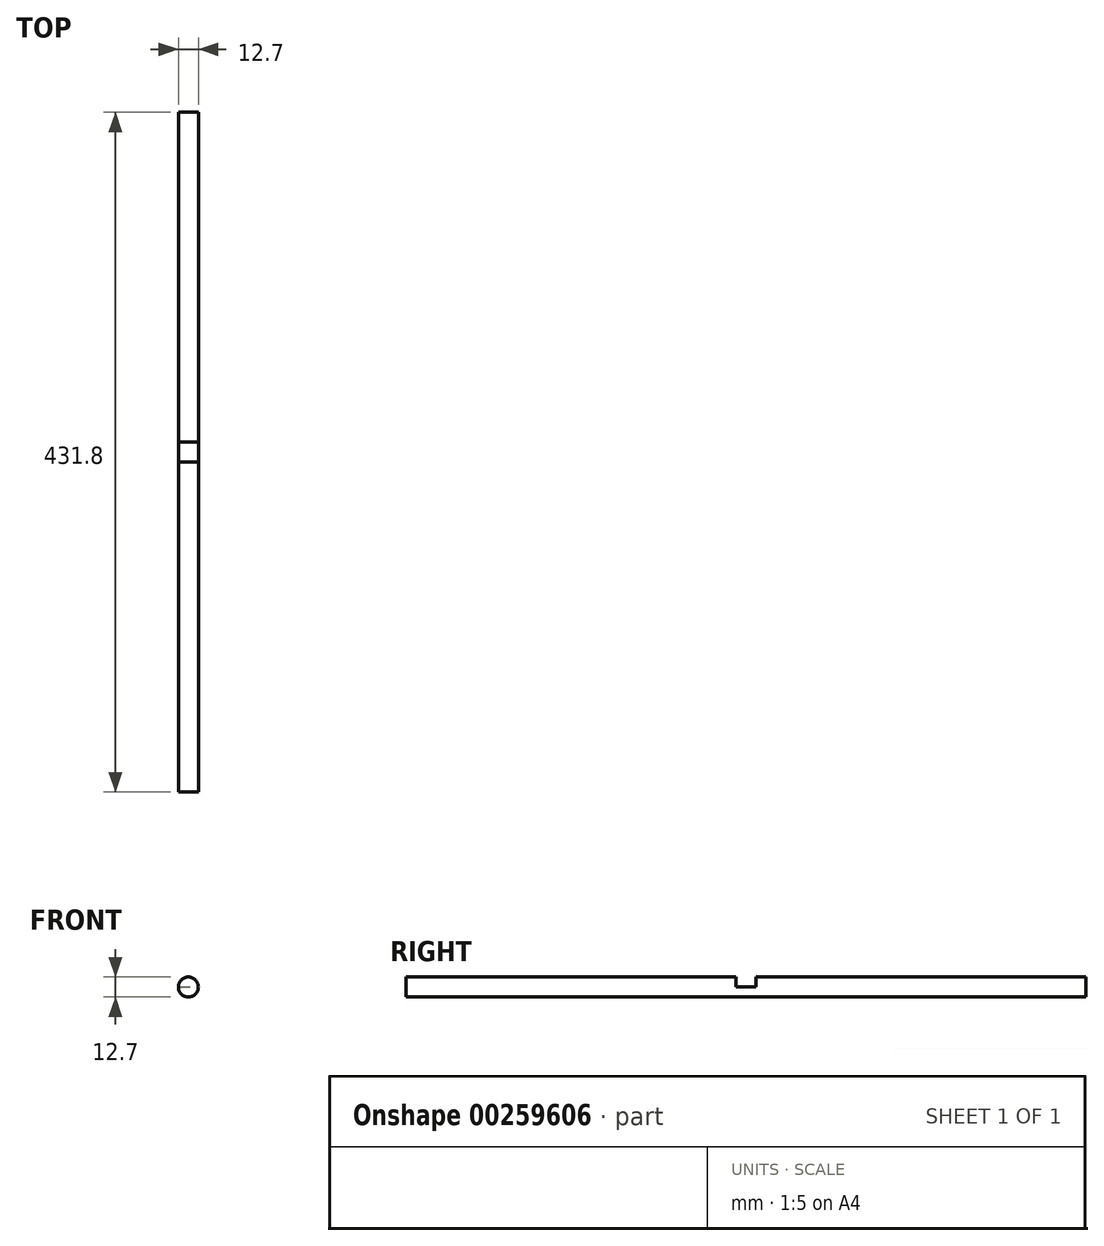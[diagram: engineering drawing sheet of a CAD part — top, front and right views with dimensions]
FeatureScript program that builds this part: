
annotation { "Feature Type Name" : "Feature", "Feature Type Description" : "" }
export const myFeature = defineFeature(function(context is Context, id is Id, definition is map)
    precondition{}
    {
        {
            var Q0;
            Q0=qCreatedBy(makeId("Front.planeOp"),FACE);
            var sketch = newSketch(context, id + "F0", { "sketchPlane" : qUnion([Q0])});
            skCircle(sketch, "E0", {"center": v(0, 0) * mm, "radius": 6.35 * mm});
            skSolve(sketch);
        }
        {
            var Q0;
            Q0=makeQuery(id+"F0.imprint","IMPRINT",FACE,{"disambiguationData":[TD([[makeQuery(id+"F0.imprint","IMPRINT",EDGE,{"derivedFrom":sQuery(id+"F0.wireOp",EDGE,"E0")}),1.0]])]});
            extrude(context, id + "F1", {"entities" : qUnion([Q0]), "depth" : 431.8 * mm, "symmetric" : true});
        }
        {
            var Q0;
            Q0=qCreatedBy(makeId("Right.planeOp"),FACE);
            var sketch = newSketch(context, id + "F2", { "sketchPlane" : qUnion([Q0])});
            skLineSegment(sketch, "E1.bottom", {"start": v(6.35, 12.7) * mm, "end": v(-6.35, 12.7) * mm});
            skLineSegment(sketch, "E1.top", {"start": v(6.35, 0) * mm, "end": v(-6.35, 0) * mm});
            skLineSegment(sketch, "E1.left", {"start": v(6.35, 12.7) * mm, "end": v(6.35, 0) * mm});
            skLineSegment(sketch, "E1.right", {"start": v(-6.35, 12.7) * mm, "end": v(-6.35, 0) * mm});
            skPoint(sketch, "E1.middle", {"position": v(0, 6.35) * mm});
            skSolve(sketch);
        }
        {
            var Q0;
            Q0=makeQuery(id+"F2.imprint","IMPRINT",FACE,{"disambiguationData":[TD([[makeQuery(id+"F2.imprint","IMPRINT",EDGE,{"derivedFrom":sQuery(id+"F2.wireOp",EDGE,"E1.bottom")}),1.0]])]});
            extrude(context, id + "F3", {"entities" : qUnion([Q0]), "operationType" : NewBodyOperationType.REMOVE, "oppositeDirection" : true, "depth" : 25.4 * mm, "symmetric" : true});
        }
    });
